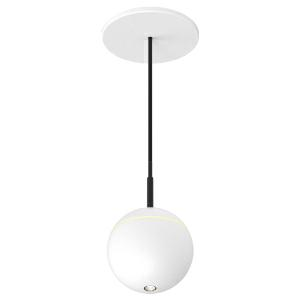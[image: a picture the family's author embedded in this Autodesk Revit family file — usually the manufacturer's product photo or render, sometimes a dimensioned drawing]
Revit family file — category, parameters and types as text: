
# Revit family: snooker_420-2700
name_source: partatom
category: Lighting Fixtures
units: mm (PartAtom-declared; Revit-internal decimal feet)

## family parameters
Cut with Voids When Loaded = No
Host = Face
Light Source = No
Part Type = Normal
Room Calculation Point = No
Round Connector Dimension = Use Diameter
Shared = No

## types (1)
- 420-2700-H27-L00-W33 (1 x LED, 460.09 lm, 6.4 W, 2700K)
    Apparent Load = 6 VA
    CIE Flux Codes = 100 100 100 100 62
    Color Rendering = 1A/90…99
    Color Temperature = 2700K
    Default Elevation = 1800 mm
    Description = SNOOKER
    Height = 72 mm  [stored 0.23622 ft]
    Lamp = 1 x LED
    Lamp Light Flux = 460.09 lm
    Lamp Power = 6.4 W
    Lamp count = 1
    Length = 72 mm  [stored 0.23622 ft]
    Luminous efficacy = 44 lm/W
    Manufacturer = Prolicht
    ModVariant = No
    Model = 420-2700
    Mounting Place = Ceiling
    Mounting Type = Pendant
    Number of Poles = 1
    OnlyDefault = Yes
    Power Factor = 1
    Product Name = SNOOKER
    Product group = Suspended spotlights
    ProductGroupID = 942
    Protection Class = Protection class
    Protection Degree = Degree of protection
    RLX_Detail_Level = 1
    RlxData = <blob elided: 88897 chars, md5=a04eb635>
    Socket = socket
    Standby Power = 0 W
    System Light Flux = 283 lm
    System Power = 6 W
    Type Comments = LED COLOUR DIR 2700 K (27),SHINE RING ABSICHTLICH_LEER (00),BEAMWIDTH Medium (33)
    Type Image = 420-2700.jpg
    URL = http://relux.com
    VarID = 420-2700-h27-l00-w33
    Voltage = 0 V
    Weight = 0.00 kg
    Width = 0 mm  [stored 0 ft]

note: [stored X ft] marks values corroborated as IEEE doubles in the binary element streams (Revit-internal decimal feet)

## geometry (parser evidence)
native form markers: Blend x4, Sweep x11
no freeform markers — native parametric forms only
